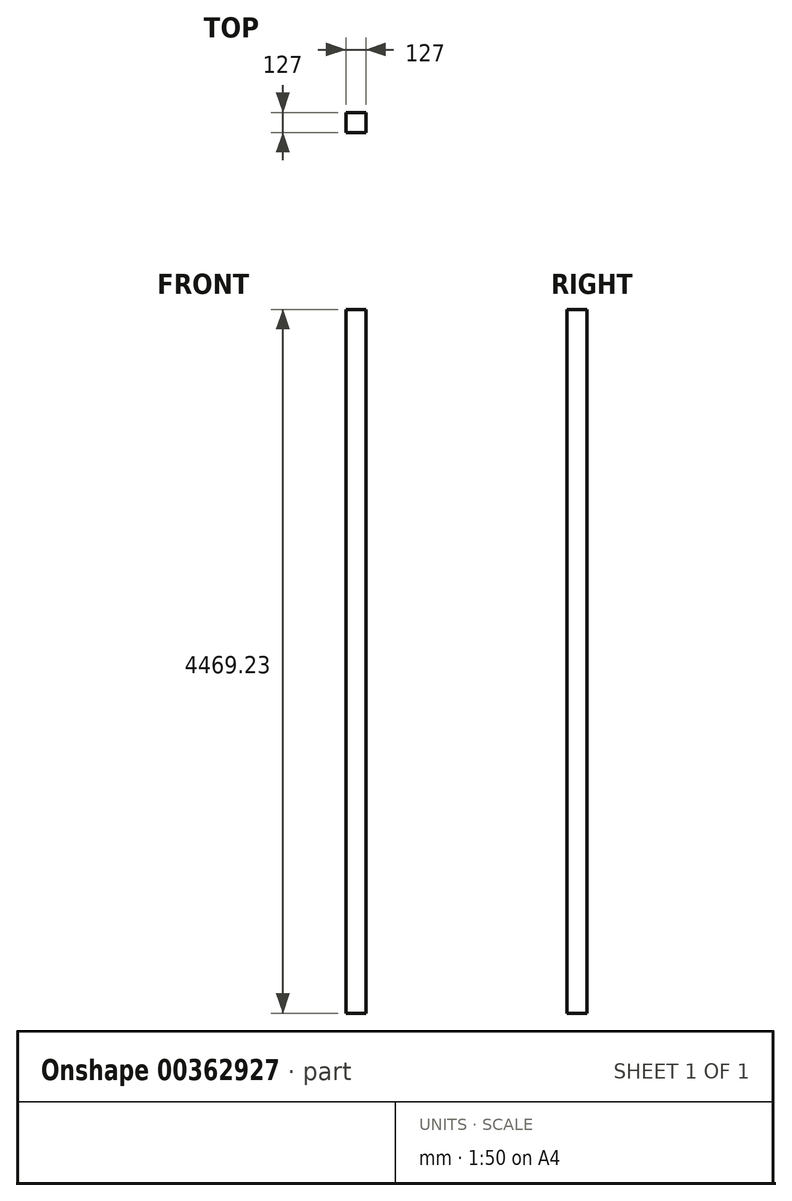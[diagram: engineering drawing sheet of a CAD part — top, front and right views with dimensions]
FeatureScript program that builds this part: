
annotation { "Feature Type Name" : "Feature", "Feature Type Description" : "" }
export const myFeature = defineFeature(function(context is Context, id is Id, definition is map)
    precondition{}
    {
        {
            var Q0;
            Q0=qCreatedBy(makeId("Front.planeOp"),FACE);
            cPlane(context, id + "F0", {"entities" : qUnion([Q0]), "cplaneType" : CPlaneType.OFFSET, "offset" : 25.4 * mm, "width" : 152.4 * mm, "height" : 152.4 * mm});
        }
        {
            var Q0;
            Q0=qCreatedBy(id+"F0.planeOp",FACE);
            var sketch = newSketch(context, id + "F1", { "sketchPlane" : qUnion([Q0])});
            skLineSegment(sketch, "E0", {"start": v(0, 0) * mm, "end": v(0, 202.03) * mm});
            skSolve(sketch);
        }
        {
            var Q0;
            Q0=sQuery(id+"F1.wireOp",EDGE,"E0");
            extrude(context, id + "F2", {"bodyType" : ToolBodyType.SURFACE, "surfaceEntities" : qUnion([Q0]), "depth" : 127 * mm});
        }
        {
            var Q0;
            Q0=makeQuery(id+"F2.opExtrude","SWEPT_FACE",FACE,{"disambiguationData":[OSD([sQuery(id+"F1.wireOp",EDGE,"E0")])]});
            extrude(context, id + "F3", {"entities" : qUnion([Q0]), "depth" : 127 * mm});
        }
        {
            var Q0;
            Q0=makeQuery(id+"F3.opExtrude","SWEPT_FACE",FACE,{"disambiguationData":[OSD([sQuery(id+"F1.wireOp",VERTEX,"E0.end")])]});
            extrude(context, id + "F4", {"entities" : qUnion([Q0]), "operationType" : NewBodyOperationType.ADD, "depth" : 4267.2 * mm});
        }
        {
            var Q0;
            Q0=makeQuery(id+"F4.opExtrude","CAP_FACE",FACE,{"disambiguationData":[OSD([sQuery(id+"F1.wireOp",VERTEX,"E0.end")])],"isStart":false});
            var sketch = newSketch(context, id + "F5", { "sketchPlane" : qUnion([Q0])});
            skLineSegment(sketch, "E1", {"start": v(419.5, 0) * mm, "end": v(67.32, -15.86) * mm});
            skSolve(sketch);
        }
        {
            var Q0;
            {var subQ0=sQuery(id+"F1.wireOp",VERTEX,"E0.end");Q0=makeQuery(id+"F5.imprint","IMPRINT",FACE,{"disambiguationData":[TD([[makeQuery(id+"F5.imprint","IMPRINT",EDGE,{"derivedFrom":makeQuery(id+"F4.opExtrude","CAP_EDGE",EDGE,{"disambiguationData":[OSD([subQ0]),TDD([makeQuery(id+"F3.opExtrude","CAP_EDGE",EDGE,{"disambiguationData":[OSD([subQ0])],"isStart":true})])],"isStart":false})}),1.0]])]});}
            var sketch = newSketch(context, id + "F6", { "sketchPlane" : qUnion([Q0])});
            skSolve(sketch);
        }
        {
            var Q0;
            {var subQ0=sQuery(id+"F1.wireOp",VERTEX,"E0.end");Q0=makeQuery(id+"F6.imprint","IMPRINT",FACE,{"disambiguationData":[TD([[makeQuery(id+"F6.imprint","IMPRINT",EDGE,{"derivedFrom":makeQuery(id+"F5.imprint","IMPRINT",EDGE,{"derivedFrom":makeQuery(id+"F4.opExtrude","CAP_EDGE",EDGE,{"disambiguationData":[OSD([subQ0]),TDD([makeQuery(id+"F3.opExtrude","CAP_EDGE",EDGE,{"disambiguationData":[OSD([subQ0])],"isStart":true})])],"isStart":false})})}),1.0]])]});}
            var sketch = newSketch(context, id + "F7", { "sketchPlane" : qUnion([Q0])});
            skLineSegment(sketch, "E2", {"start": v(0, -449.89) * mm, "end": v(421.11, 0) * mm});
            skSolve(sketch);
        }
        {
            var Q0;
            Q0=sQuery(id+"F7.wireOp",EDGE,"E2");
            extrude(context, id + "F8", {"bodyType" : ToolBodyType.SURFACE, "surfaceEntities" : qUnion([Q0]), "oppositeDirection" : true, "depth" : 914.4 * mm});
        }
    });
